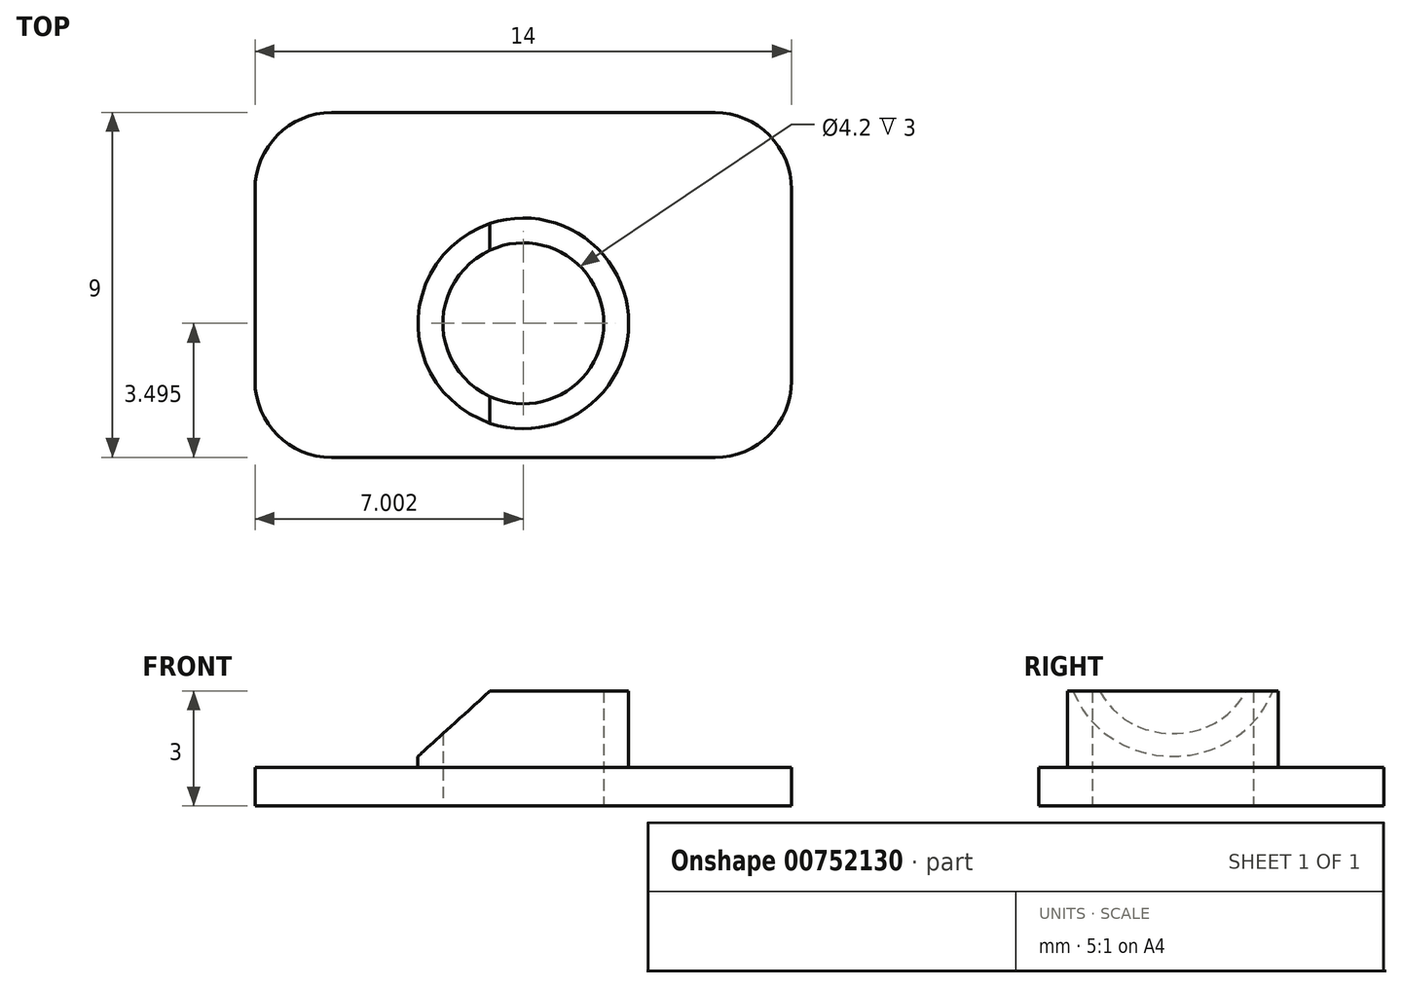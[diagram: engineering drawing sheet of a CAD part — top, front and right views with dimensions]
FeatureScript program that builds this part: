
annotation { "Feature Type Name" : "Feature", "Feature Type Description" : "" }
export const myFeature = defineFeature(function(context is Context, id is Id, definition is map)
    precondition{}
    {
        {
            var Q0;
            Q0=qCreatedBy(makeId("Top.planeOp"),FACE);
            var sketch = newSketch(context, id + "F0", { "sketchPlane" : qUnion([Q0])});
            skLineSegment(sketch, "E0.bottom", {"start": v(-6.1, 16.32) * mm, "end": v(7.9, 16.32) * mm});
            skLineSegment(sketch, "E0.top", {"start": v(-6.1, 7.32) * mm, "end": v(7.9, 7.32) * mm});
            skLineSegment(sketch, "E0.left", {"start": v(-6.1, 16.32) * mm, "end": v(-6.1, 7.32) * mm});
            skLineSegment(sketch, "E0.right", {"start": v(7.9, 16.32) * mm, "end": v(7.9, 7.32) * mm});
            skSolve(sketch);
        }
        {
            var Q0;
            Q0 = qSketchRegion(id + "F0", true);
            extrude(context, id + "F1", {"entities" : qUnion([Q0]), "depth" : 1 * mm, "offsetDistance" : 25 * mm});
        }
        {
            var Q0;
            Q0=makeQuery(id+"F1.opExtrude","CAP_FACE",FACE,{"disambiguationData":[OSD([sQuery(id+"F0.wireOp",EDGE,"E0.bottom"),sQuery(id+"F0.wireOp",EDGE,"E0.top"),sQuery(id+"F0.wireOp",EDGE,"E0.left"),sQuery(id+"F0.wireOp",EDGE,"E0.right")])],"isStart":false});
            var sketch = newSketch(context, id + "F2", { "sketchPlane" : qUnion([Q0])});
            skCircle(sketch, "E1", {"center": v(0.9, 10.82) * mm, "radius": 2.1 * mm});
            skCircle(sketch, "E2", {"center": v(0.9, 10.82) * mm, "radius": 2.75 * mm});
            skSolve(sketch);
        }
        {
            var Q0;
            Q0=makeQuery(id+"F2.imprint","IMPRINT",FACE,{"disambiguationData":[TD([[makeQuery(id+"F2.imprint","IMPRINT",EDGE,{"derivedFrom":sQuery(id+"F2.wireOp",EDGE,"E1")}),-1.0]])]});
            extrude(context, id + "F3", {"entities" : qUnion([Q0]), "operationType" : NewBodyOperationType.ADD, "depth" : 2 * mm, "offsetDistance" : 25 * mm});
        }
        {
            var Q0;
            Q0=makeQuery(id+"F3.boolean.opBoolean","SPLIT",FACE,{"disambiguationData":[TD([makeQuery(id+"F3.opExtrude","SWEPT_FACE",FACE,{"disambiguationData":[OSD([sQuery(id+"F2.wireOp",EDGE,"E1")])]})])],"derivedFrom":makeQuery(id+"F1.opExtrude","CAP_FACE",FACE,{"disambiguationData":[OSD([sQuery(id+"F0.wireOp",EDGE,"E0.bottom"),sQuery(id+"F0.wireOp",EDGE,"E0.top"),sQuery(id+"F0.wireOp",EDGE,"E0.left"),sQuery(id+"F0.wireOp",EDGE,"E0.right")])],"isStart":false})});
            extrude(context, id + "F4", {"entities" : qUnion([Q0]), "operationType" : NewBodyOperationType.REMOVE, "oppositeDirection" : true, "depth" : 1.5 * mm, "offsetDistance" : 25 * mm});
        }
        {
            var Q0;
            Q0=makeQuery(id+"F1.opExtrude","SWEPT_EDGE",EDGE,{"disambiguationData":[OSD([sQuery(id+"F0.wireOp",EDGE,"E0.top"),sQuery(id+"F0.wireOp",EDGE,"E0.left")])]});
            var Q1;
            Q1=makeQuery(id+"F1.opExtrude","SWEPT_EDGE",EDGE,{"disambiguationData":[OSD([sQuery(id+"F0.wireOp",EDGE,"E0.bottom"),sQuery(id+"F0.wireOp",EDGE,"E0.left")])]});
            var Q2;
            Q2=makeQuery(id+"F1.opExtrude","SWEPT_EDGE",EDGE,{"disambiguationData":[OSD([sQuery(id+"F0.wireOp",EDGE,"E0.top"),sQuery(id+"F0.wireOp",EDGE,"E0.right")])]});
            var Q3;
            Q3=makeQuery(id+"F1.opExtrude","SWEPT_EDGE",EDGE,{"disambiguationData":[OSD([sQuery(id+"F0.wireOp",EDGE,"E0.bottom"),sQuery(id+"F0.wireOp",EDGE,"E0.right")])]});
            fillet(context, id + "F5", {"entities" : qUnion([Q0, Q1, Q2, Q3]), "radius" : 2 * mm, "tangentPropagation" : true, "allowEdgeOverflow" : false});
        }
        {
            var Q0;
            Q0=makeQuery(id+"F1.opExtrude","SWEPT_FACE",FACE,{"disambiguationData":[OSD([sQuery(id+"F0.wireOp",EDGE,"E0.top")])]});
            var sketch = newSketch(context, id + "F6", { "sketchPlane" : qUnion([Q0])});
            skLineSegment(sketch, "E3.left", {"start": v(-2.17, 3.45) * mm, "end": v(-2.17, 1) * mm});
            skLineSegment(sketch, "E4", {"start": v(-2.17, 1) * mm, "end": v(0.52, 3.45) * mm});
            skLineSegment(sketch, "E5", {"start": v(-2.17, 3.45) * mm, "end": v(0.52, 3.45) * mm});
            skSolve(sketch);
        }
        {
            var Q0;
            Q0=makeQuery(id+"F6.imprint","IMPRINT",FACE,{"disambiguationData":[TD([[makeQuery(id+"F6.imprint","IMPRINT",EDGE,{"derivedFrom":sQuery(id+"F6.wireOp",EDGE,"E3.left")}),1.0]])]});
            extrude(context, id + "F7", {"entities" : qUnion([Q0]), "operationType" : NewBodyOperationType.REMOVE, "oppositeDirection" : true, "depth" : 25 * mm, "offsetDistance" : 25 * mm});
        }
    });
